# Revit family: Magnuson-Sherwood-CoatHookStrip+
name_source: partatom
category: Furniture
units: mm (PartAtom-declared; Revit-internal decimal feet)

## family parameters
Cut with Voids When Loaded = No
Host = Face
Room Calculation Point = No
Shared = No

## types (3) — shared parameters
Assembly Code = E2020200
Default Elevation = 48"
Frame Finish = MAG - Textured painted steel
Hook Finish = MAG - Wood Oak
Hook2 Qty = 2
Keynote = 12500
Low Emitting Finish = Yes
Low Emitting Material = Yes
Manufacturer = Magnuson Group
Product Documentation Link = https://magnusongroup.com
Revit Model Built By = https://servex-us.com
Salvage or Reuse = Yes
Type Comments = Coat Hook Strip
URL = www.magnusongroup.com
zero-valued in all types: Percentage of Recycled Content

## per-type parameters (varying)
| type | Description | H | H2 Dist | H2 End Dist | Hook Qty | Width |
| SW-M2 | Painted metal hook strip with two wood hooks positioned horizontally | No | 0" | 4 1/8" | 2 | 8 9/32" |
| SW-M3 | Painted metal hook strip with three wood hooks. Center hook is positioned vertically, two outer hooks are positioned horizontally. | Yes | 0" | 7 15/32" | 2 | 14 31/32" |
| SW-M5 | Painted metal hook strip with five wood hooks. Hooks alternate between horizontal and vertical positioning. | Yes | 13 3/8" | 7 15/32" | 3 | 28 11/32" |

note: column(s) folded — value = type name in every type: Model

## geometry (parser evidence)
native form markers: Sweep x5
no freeform markers — native parametric forms only
